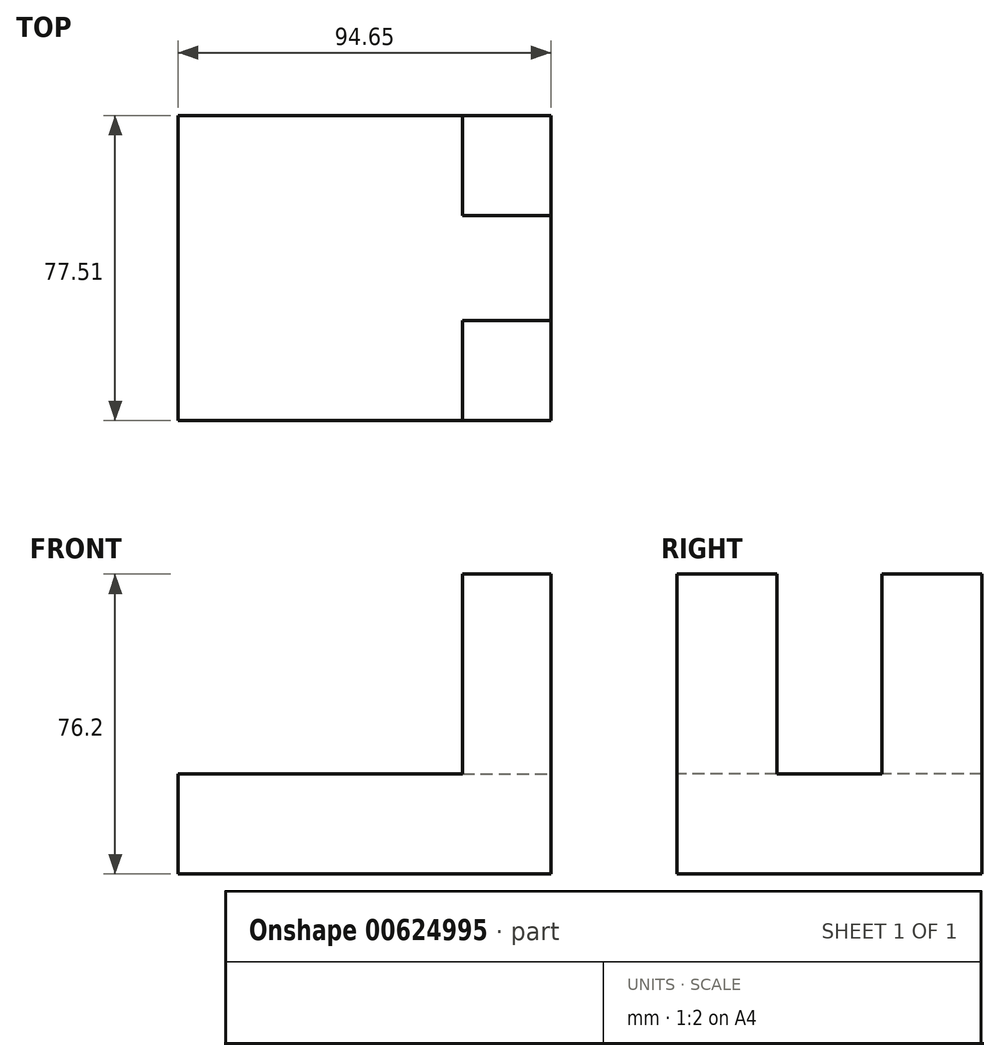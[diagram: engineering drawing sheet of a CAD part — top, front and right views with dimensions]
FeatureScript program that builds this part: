
annotation { "Feature Type Name" : "Feature", "Feature Type Description" : "" }
export const myFeature = defineFeature(function(context is Context, id is Id, definition is map)
    precondition{}
    {
        {
            var Q0;
            Q0=qCreatedBy(makeId("Top.planeOp"),FACE);
            var sketch = newSketch(context, id + "F0", { "sketchPlane" : qUnion([Q0])});
            skLineSegment(sketch, "E0", {"start": v(-45.18, 39.11) * mm, "end": v(-45.18, -38.4) * mm});
            skLineSegment(sketch, "E1", {"start": v(-45.18, -38.4) * mm, "end": v(49.47, -38.4) * mm});
            skLineSegment(sketch, "E2", {"start": v(49.47, -38.4) * mm, "end": v(49.47, 39.11) * mm});
            skLineSegment(sketch, "E3", {"start": v(-45.18, 39.11) * mm, "end": v(49.47, 39.11) * mm});
            skSolve(sketch);
        }
        {
            var Q0;
            Q0 = qSketchRegion(id + "F0", true);
            extrude(context, id + "F1", {"entities" : qUnion([Q0]), "depth" : 25.4 * mm, "offsetDistance" : 25.4 * mm});
        }
        {
            var Q0;
            Q0=makeQuery(id+"F1.opExtrude","CAP_FACE",FACE,{"disambiguationData":[OSD([sQuery(id+"F0.wireOp",EDGE,"E0"),sQuery(id+"F0.wireOp",EDGE,"E1"),sQuery(id+"F0.wireOp",EDGE,"E2"),sQuery(id+"F0.wireOp",EDGE,"E3")])],"isStart":false});
            var sketch = newSketch(context, id + "F2", { "sketchPlane" : qUnion([Q0])});
            skLineSegment(sketch, "E4.bottom", {"start": v(49.47, 39.11) * mm, "end": v(30.48, 39.11) * mm});
            skLineSegment(sketch, "E4.left", {"start": v(49.47, 39.11) * mm, "end": v(49.47, 13.71) * mm});
            skLineSegment(sketch, "E5.bottom", {"start": v(49.47, 39.11) * mm, "end": v(27.06, 39.11) * mm});
            skLineSegment(sketch, "E5.top", {"start": v(49.47, -38.4) * mm, "end": v(27.06, -38.4) * mm});
            skLineSegment(sketch, "E5.left", {"start": v(49.47, 39.11) * mm, "end": v(49.47, -38.4) * mm});
            skLineSegment(sketch, "E5.right", {"start": v(27.06, 39.11) * mm, "end": v(27.06, 13.71) * mm});
            skLineSegment(sketch, "E6", {"start": v(49.47, 13.71) * mm, "end": v(27.06, 13.71) * mm});
            skLineSegment(sketch, "E7", {"start": v(27.06, -13) * mm, "end": v(49.47, -13) * mm});
            skLineSegment(sketch, "E8.trimOffspring", {"start": v(27.06, -13) * mm, "end": v(27.06, -38.4) * mm});
            skSolve(sketch);
        }
        {
            var Q0;
            Q0 = qSketchRegion(id + "F2", true);
            extrude(context, id + "F3", {"entities" : qUnion([Q0]), "operationType" : NewBodyOperationType.ADD, "depth" : 50.8 * mm, "offsetDistance" : 25.4 * mm});
        }
    });
